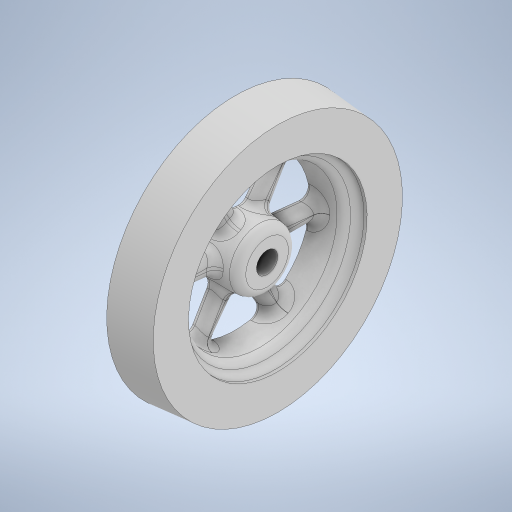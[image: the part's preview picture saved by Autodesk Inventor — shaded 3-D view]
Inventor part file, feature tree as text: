
AUTODESK INVENTOR PART (.ipt)
format: ipt  version: 2023 (Build 270158000, 158)  size: 1,142,784 bytes
history: native  units: in
note: dims shown in document units (in); Inventor stores cm internally (conversion verified against a paired STEP export)
features: extrude x4, sketch x2, fillet x2, draft x1
ambient origin geometry x8: Origin, YZ Plane, XZ Plane, XY Plane, X Axis, Y Axis, Z Axis, Center Point
bodies: Body1 (feature_tree)
feature tree (9):
  sketch  "Sketch1"  dims[d29=0.125in d31=2.0in d32=3.0in]
  extrude  "Extrusion7"  Depth=3.0in
  extrude  "Extrusion8"  Depth=0.25in
  extrude  "Extrusion9"  Depth=1.75in
  sketch  "Sketch3"  dims[d33=0.75in d34=0.25in d35=1.75in d37=2.3622in d39=360.0deg d41=1.0in d42=0.0in d43=0.75in d44=0.0in d45=0.25in d46=0.0in d54=0.0344in d55=0.1in d56=0.1in d57=5.0in d58=0.0in]
  draft  "FaceDraft2"
  fillet  "Fillet5"  Radius=2.3622in
  fillet  "Fillet6"  Radius=1.0in
  extrude  "Extrusion11"  Depth=0.75in TaperAngle=0.0deg
